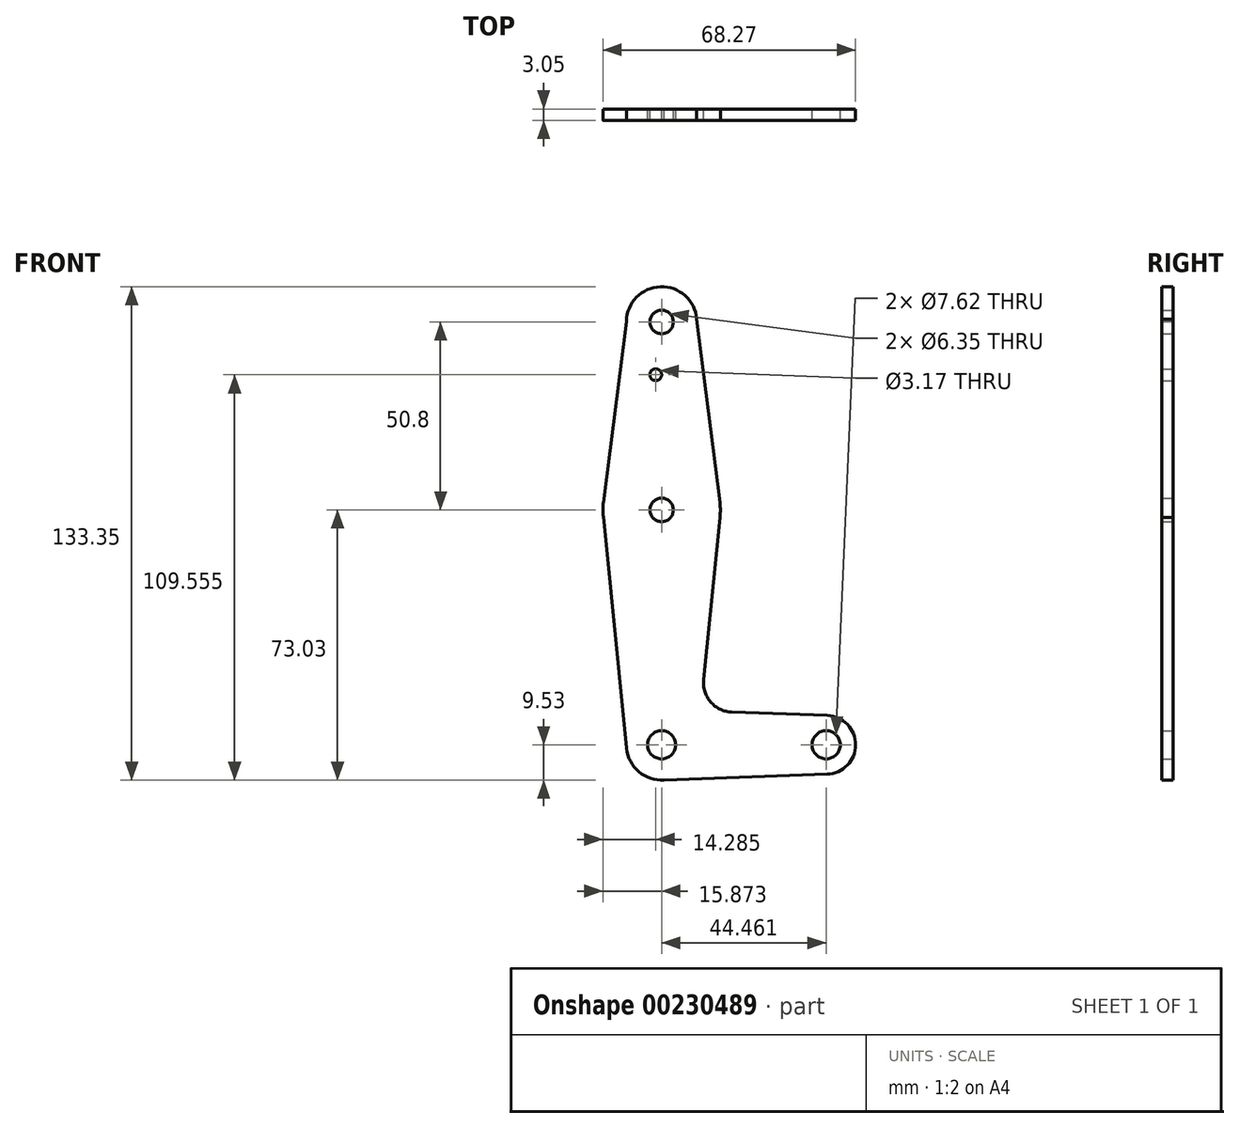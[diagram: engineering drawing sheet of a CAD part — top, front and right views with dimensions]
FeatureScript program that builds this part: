
annotation { "Feature Type Name" : "Feature", "Feature Type Description" : "" }
export const myFeature = defineFeature(function(context is Context, id is Id, definition is map)
    precondition{}
    {
        {
            var Q0;
            Q0=qCreatedBy(makeId("Front.planeOp"),FACE);
            var sketch = newSketch(context, id + "F0", { "sketchPlane" : qUnion([Q0])});
            skLineSegment(sketch, "E0", {"start": v(-58.37, 50.8) * mm, "end": v(-58.37, -63.5) * mm});
            skLineSegment(sketch, "E1", {"start": v(-58.37, -63.5) * mm, "end": v(-13.9, -63.5) * mm});
            skCircle(sketch, "E2", {"center": v(-58.37, 50.8) * mm, "radius": 9.53 * mm});
            skCircle(sketch, "E3", {"center": v(-58.37, 0) * mm, "radius": 15.88 * mm});
            skCircle(sketch, "E4", {"center": v(-58.37, -63.5) * mm, "radius": 9.53 * mm});
            skCircle(sketch, "E5", {"center": v(-13.9, -63.5) * mm, "radius": 7.94 * mm});
            skLineSegment(sketch, "E6", {"start": v(-67.9, 50.92) * mm, "end": v(-74.12, 2) * mm});
            skLineSegment(sketch, "E7", {"start": v(-74.13, -1.85) * mm, "end": v(-67.84, -64.45) * mm});
            skLineSegment(sketch, "E8", {"start": v(-48.98, 52.4) * mm, "end": v(-42.62, 1.99) * mm});
            skLineSegment(sketch, "E9", {"start": v(-42.62, -1.99) * mm, "end": v(-47.03, -45.91) * mm});
            skLineSegment(sketch, "E10", {"start": v(-39.4, -54.65) * mm, "end": v(-13.62, -55.57) * mm});
            skLineSegment(sketch, "E11", {"start": v(-58.37, -73.03) * mm, "end": v(-13.62, -71.43) * mm});
            skCircle(sketch, "E12", {"center": v(-58.37, 50.8) * mm, "radius": 3.18 * mm});
            skCircle(sketch, "E13", {"center": v(-58.37, 0) * mm, "radius": 3.18 * mm});
            skCircle(sketch, "E14", {"center": v(-58.37, -63.5) * mm, "radius": 3.81 * mm});
            skCircle(sketch, "E15", {"center": v(-13.9, -63.5) * mm, "radius": 3.81 * mm});
            skPoint(sketch, "E16.newPointB", {"position": v(-58.37, -53.98) * mm});
            skArc(sketch, "E16.filletArc", {"start": v(-47.03, -45.91) * mm, "mid": v(-45.1, -51.93) * mm, "end": v(-39.4, -54.65) * mm});
            skCircle(sketch, "E17", {"center": v(-59.95, 36.53) * mm, "radius": 1.59 * mm});
            skSolve(sketch);
        }
        {
            var Q0;
            Q0 = qSketchRegion(id + "F0", true);
            var Q1;
            {var subQ0=sQuery(id+"F0.wireOp",EDGE,"E4");var subQ1=sQuery(id+"F0.wireOp",EDGE,"E0");var subQ2=makeQuery(id+"F0.imprint","INTERSECT",VERTEX,{"derivedFrom":[subQ1,subQ0]});Q1=makeQuery(id+"F0.imprint","IMPRINT",FACE,{"disambiguationData":[TD([[makeQuery(id+"F0.imprint","IMPRINT",EDGE,{"disambiguationData":[TD([[subQ2,-1.0]])],"derivedFrom":subQ1}),1.0]])]});}
            extrude(context, id + "F1", {"entities" : qUnion([Q0, Q1]), "depth" : 3.05 * mm});
        }
    });
